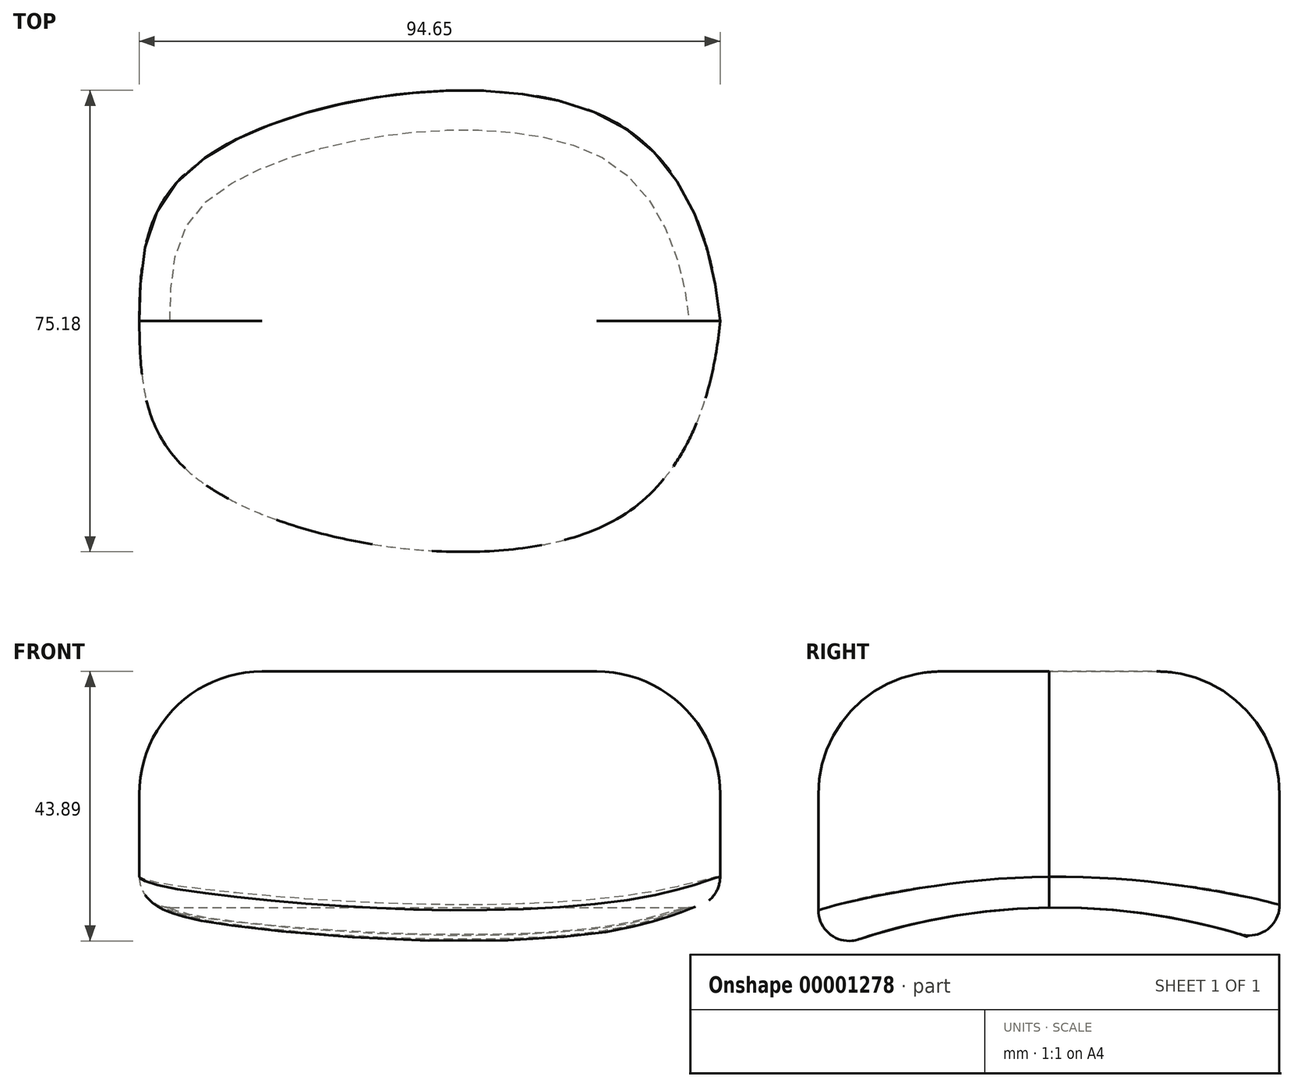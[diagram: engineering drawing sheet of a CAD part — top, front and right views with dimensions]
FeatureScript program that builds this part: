
annotation { "Feature Type Name" : "Feature", "Feature Type Description" : "" }
export const myFeature = defineFeature(function(context is Context, id is Id, definition is map)
    precondition{}
    {
        {
            var Q0;
            Q0=qCreatedBy(makeId("Top.planeOp"),FACE);
            var sketch = newSketch(context, id + "F0", { "sketchPlane" : qUnion([Q0])});
            skLineSegment(sketch, "E0.bottom", {"start": v(-45.95, 25.54) * mm, "end": v(48.7, 25.54) * mm, "construction": true});
            skLineSegment(sketch, "E0.top", {"start": v(-45.95, 0) * mm, "end": v(48.7, 0) * mm, "construction": true});
            skLineSegment(sketch, "E0.left", {"start": v(-45.95, 25.54) * mm, "end": v(-45.95, 0) * mm, "construction": true});
            skLineSegment(sketch, "E0.right", {"start": v(48.7, 25.54) * mm, "end": v(48.7, 0) * mm, "construction": true});
            skFitSpline(sketch, "E1", {"points": [v(-45.95, 0) * mm, v(-36.68, 25.54) * mm, v(31.89, 32.24) * mm, v(48.7, 0) * mm, v(48.7, -10.42) * mm], "startDerivative": vector(2.14, 121.1) * mm, "endDerivative": vector(-4.57, -59.57) * mm});
            skFitSpline(sketch, "E2.0.MirrorCS", {"points": [v(-45.95, 0) * mm, v(-36.68, -25.54) * mm, v(31.89, -32.24) * mm, v(48.7, 0) * mm, v(48.7, 10.42) * mm], "startDerivative": vector(2.14, -121.1) * mm, "endDerivative": vector(-4.57, 59.57) * mm});
            skSolve(sketch);
        }
        {
            var Q0;
            Q0=makeQuery(id+"F0.imprint","IMPRINT",FACE,{"disambiguationData":[TD([[makeQuery(id+"F0.imprint","IMPRINT",EDGE,{"derivedFrom":sQuery(id+"F0.wireOp",EDGE,"E1")}),-1.0]])]});
            extrude(context, id + "F1", {"entities" : qUnion([Q0]), "depth" : 43.93 * mm});
        }
        {
            var Q0;
            Q0=makeQuery(id+"F1.opExtrude","CAP_EDGE",EDGE,{"disambiguationData":[OSD([sQuery(id+"F0.wireOp",EDGE,"E1")])],"isStart":false});
            var Q1;
            Q1=makeQuery(id+"F1.opExtrude","CAP_EDGE",EDGE,{"disambiguationData":[OSD([sQuery(id+"F0.wireOp",EDGE,"E2.0.MirrorCS")])],"isStart":false});
            fillet(context, id + "F2", {"entities" : qUnion([Q0, Q1]), "radius" : 20 * mm, "tangentPropagation" : true, "allowEdgeOverflow" : false});
        }
        {
            var Q0;
            Q0=qCreatedBy(makeId("Right.planeOp"),FACE);
            var sketch = newSketch(context, id + "F3", { "sketchPlane" : qUnion([Q0])});
            skArc(sketch, "E3", {"start": v(50, -6.6) * mm, "mid": v(-0.2, 5.47) * mm, "end": v(-50, -8.12) * mm});
            skLineSegment(sketch, "E4", {"start": v(50, -6.6) * mm, "end": v(-50, -8.12) * mm});
            skSolve(sketch);
        }
        {
            var Q0;
            Q0=makeQuery(id+"F3.imprint","IMPRINT",FACE,{"disambiguationData":[TD([[makeQuery(id+"F3.imprint","IMPRINT",EDGE,{"derivedFrom":sQuery(id+"F3.wireOp",EDGE,"E3")}),1.0]])]});
            var Q1;
            Q1=sQuery(id+"F3.wireOp",EDGE,"E4");
            extrude(context, id + "F4", {"entities" : qUnion([Q0]), "operationType" : NewBodyOperationType.REMOVE, "surfaceEntities" : qUnion([Q1]), "oppositeDirection" : true, "depth" : 100 * mm, "symmetric" : true});
        }
        {
            var Q0;
            Q0=makeQuery(id+"F4.boolean.opBoolean","INTERSECT",EDGE,{"disambiguationData":[OD(0.0)],"derivedFrom":[makeQuery(id+"F1.opExtrude","SWEPT_FACE",FACE,{"disambiguationData":[OSD([sQuery(id+"F0.wireOp",EDGE,"E2.0.MirrorCS")])]}),makeQuery(id+"F4.opExtrude","SWEPT_FACE",FACE,{"disambiguationData":[OSD([sQuery(id+"F3.wireOp",EDGE,"E3")])]})]});
            var Q1;
            Q1=makeQuery(id+"F4.boolean.opBoolean","INTERSECT",EDGE,{"disambiguationData":[OD(0.0)],"derivedFrom":[makeQuery(id+"F1.opExtrude","SWEPT_FACE",FACE,{"disambiguationData":[OSD([sQuery(id+"F0.wireOp",EDGE,"E1")])]}),makeQuery(id+"F4.opExtrude","SWEPT_FACE",FACE,{"disambiguationData":[OSD([sQuery(id+"F3.wireOp",EDGE,"E3")])]})]});
            fillet(context, id + "F5", {"entities" : qUnion([Q0, Q1]), "radius" : 5 * mm, "tangentPropagation" : true, "allowEdgeOverflow" : false});
        }
    });
